# Revit family: CRD09304-BK
name_source: partatom
category: Lighting Fixtures
units: mm (PartAtom-declared; Revit-internal decimal feet)

## family parameters
Always vertical = Yes
Cut with Voids When Loaded = No
Light Source = Yes
Part Type = Normal
Room Calculation Point = No
Round Connector Dimension = Use Diameter
Shared = No
Work Plane-Based = No

## types (1)
- CRD09304-BK
    Apparent Load = 10 VA
    Body Colour = BLACK
    Body Material = <By Category>
    CRI = 80
    Catalog Number = CRD09304-BK
    Color Filter = 16777215
    Default Elevation = 0' - 0"
    Description = CYLINDER LED WALL LIGHT Down Light
    Dimming = NON DIMMING
    Dimming Lamp Color Temperature Shift = <None>
    Fixture Diameter = 0' - 4 1/4"
    Fixture Height = 0' - 7 7/8"
    IES File URL = https://www.abovealllighting.com
    Inside body material = <By Category>
    Lamp = LED
    Life = L70-100,000 HOURS
    Load Classification = Lighting
    Manufacturer = Above All Lighting
    Model = CRD09304-BK
    Photometric Web File = CRD09304-BK_IESNA2002.IES
    Power Factor = 0.87
    Specification Sheet URL = www.abovealllighting.com/Uploads/files/202305/CylinderDownWL20230512.pdf
    Tilt Angle = 90.00°
    URL = www.abovealllighting.com
    Voltage = 120 V
    Wattage Comments = 9W

## geometry (parser evidence)
native form markers: Sweep x3
no freeform markers — native parametric forms only
